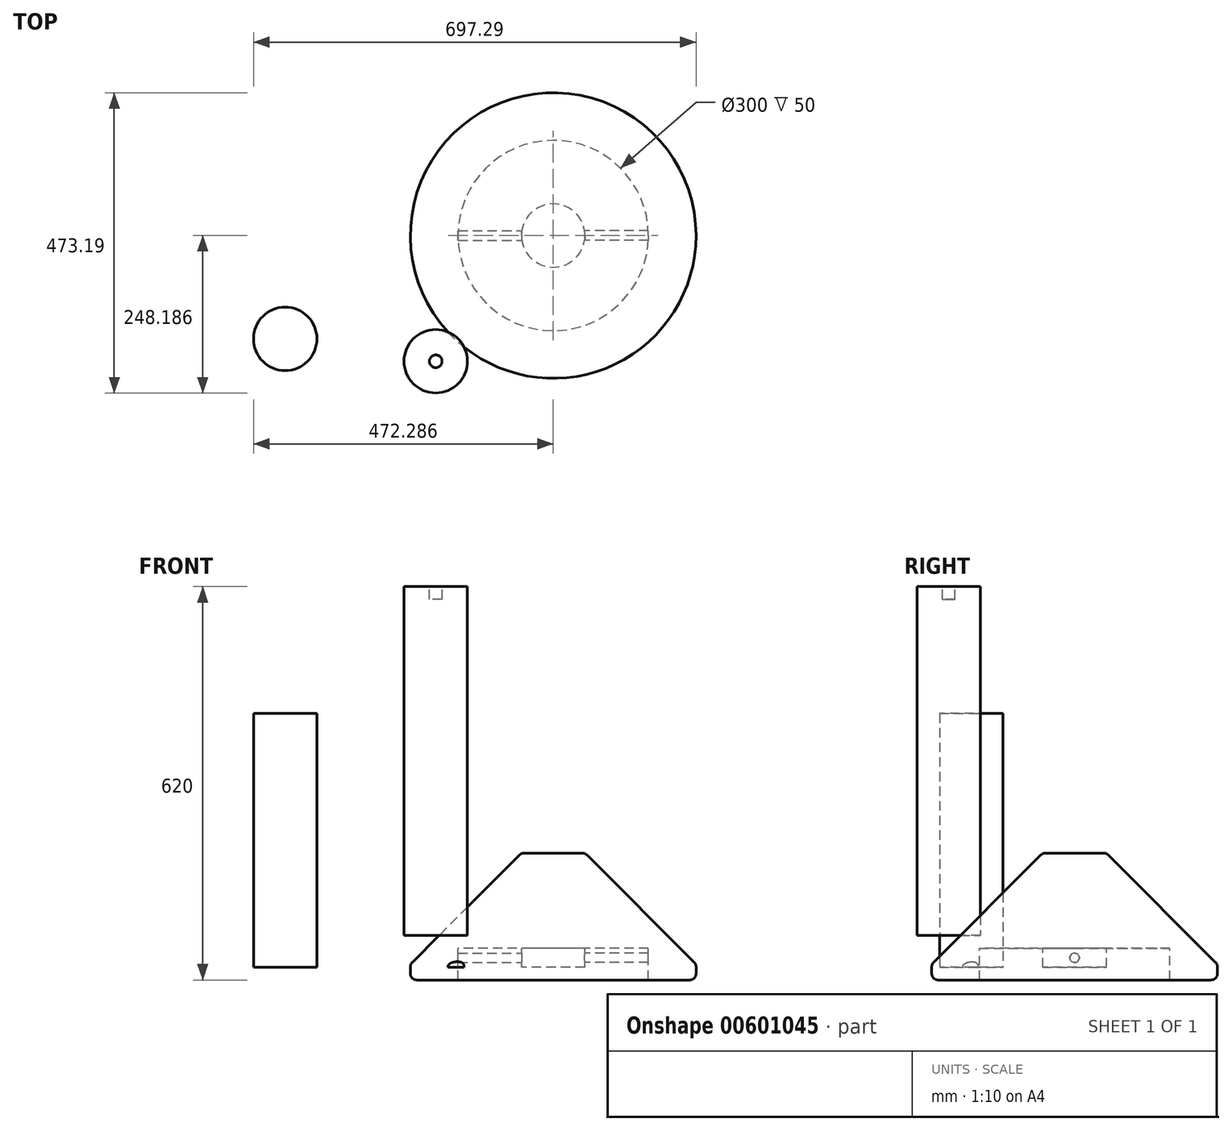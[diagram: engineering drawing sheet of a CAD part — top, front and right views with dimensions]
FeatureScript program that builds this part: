
annotation { "Feature Type Name" : "Feature", "Feature Type Description" : "" }
export const myFeature = defineFeature(function(context is Context, id is Id, definition is map)
    precondition{}
    {
        {
            var Q0;
            Q0=qCreatedBy(makeId("Top.planeOp"),FACE);
            var sketch = newSketch(context, id + "F0", { "sketchPlane" : qUnion([Q0])});
            skCircle(sketch, "E0", {"center": v(-98.02, -16.02) * mm, "radius": 50 * mm});
            skCircle(sketch, "E1", {"center": v(-335.22, 19.35) * mm, "radius": 50 * mm});
            skLineSegment(sketch, "E2.bottom", {"start": v(37.07, 232.17) * mm, "end": v(137.07, 232.17) * mm});
            skLineSegment(sketch, "E2.top", {"start": v(37.07, 132.17) * mm, "end": v(137.07, 132.17) * mm});
            skLineSegment(sketch, "E2.left", {"start": v(37.07, 232.17) * mm, "end": v(37.07, 132.17) * mm});
            skLineSegment(sketch, "E2.right", {"start": v(137.07, 232.17) * mm, "end": v(137.07, 132.17) * mm});
            skSolve(sketch);
        }
        {
            var Q0;
            Q0=makeQuery(id+"F0.imprint","IMPRINT",FACE,{"disambiguationData":[TD([[makeQuery(id+"F0.imprint","IMPRINT",EDGE,{"derivedFrom":sQuery(id+"F0.wireOp",EDGE,"E0")}),1.0]])]});
            extrude(context, id + "F1", {"entities" : qUnion([Q0]), "depth" : 600 * mm, "offsetDistance" : 25 * mm});
        }
        {
            var Q0;
            Q0=makeQuery(id+"F1.opExtrude","CAP_FACE",FACE,{"disambiguationData":[OSD([sQuery(id+"F0.wireOp",EDGE,"E0")])],"isStart":false});
            var sketch = newSketch(context, id + "F2", { "sketchPlane" : qUnion([Q0])});
            skCircle(sketch, "E3", {"center": v(-98.02, -16.02) * mm, "radius": 10 * mm});
            skSolve(sketch);
        }
        {
            var Q0;
            Q0 = qSketchRegion(id + "F2", true);
            extrude(context, id + "F3", {"entities" : qUnion([Q0]), "operationType" : NewBodyOperationType.REMOVE, "oppositeDirection" : true, "depth" : 20 * mm, "offsetDistance" : 25 * mm});
        }
        {
            var Q0;
            Q0=makeQuery(id+"F0.imprint","IMPRINT",FACE,{"disambiguationData":[TD([[makeQuery(id+"F0.imprint","IMPRINT",EDGE,{"derivedFrom":sQuery(id+"F0.wireOp",EDGE,"E1")}),1.0]])]});
            extrude(context, id + "F4", {"entities" : qUnion([Q0]), "depth" : 400 * mm, "offsetDistance" : 25 * mm});
        }
        {
            var Q0;
            Q0=makeQuery(id+"F0.imprint","IMPRINT",FACE,{"disambiguationData":[TD([[makeQuery(id+"F0.imprint","IMPRINT",EDGE,{"derivedFrom":sQuery(id+"F0.wireOp",EDGE,"E2.bottom")}),-1.0]])]});
            extrude(context, id + "F5", {"entities" : qUnion([Q0]), "depth" : 30 * mm, "offsetDistance" : 25 * mm});
        }
        {
            var Q0;
            Q0=makeQuery(id+"F5.opExtrude","SWEPT_FACE",FACE,{"disambiguationData":[OSD([sQuery(id+"F0.wireOp",EDGE,"E2.right")])]});
            var sketch = newSketch(context, id + "F6", { "sketchPlane" : qUnion([Q0])});
            skCircle(sketch, "E4", {"center": v(182.17, 15) * mm, "radius": 7.5 * mm});
            skPoint(sketch, "E4.centerSnap0", {"position": v(132.17, 15) * mm});
            skPoint(sketch, "E4.centerSnap1", {"position": v(182.17, 0) * mm});
            skSolve(sketch);
        }
        {
            var Q0;
            Q0 = qSketchRegion(id + "F6", true);
            extrude(context, id + "F7", {"entities" : qUnion([Q0]), "operationType" : NewBodyOperationType.ADD, "oppositeDirection" : true, "depth" : 200 * mm, "offsetDistance" : 25 * mm});
        }
        {
            var Q0;
            Q0=makeQuery(id+"F6.imprint","IMPRINT",FACE,{"disambiguationData":[TD([[makeQuery(id+"F6.imprint","IMPRINT",EDGE,{"derivedFrom":sQuery(id+"F6.wireOp",EDGE,"E4")}),1.0]])]});
            extrude(context, id + "F8", {"entities" : qUnion([Q0]), "operationType" : NewBodyOperationType.ADD, "depth" : 100 * mm, "offsetDistance" : 25 * mm});
        }
        {
            var Q0;
            Q0=makeQuery(id+"F5.opExtrude","CAP_FACE",FACE,{"disambiguationData":[OSD([sQuery(id+"F0.wireOp",EDGE,"E2.bottom"),sQuery(id+"F0.wireOp",EDGE,"E2.top"),sQuery(id+"F0.wireOp",EDGE,"E2.left"),sQuery(id+"F0.wireOp",EDGE,"E2.right")])],"isStart":false});
            var sketch = newSketch(context, id + "F9", { "sketchPlane" : qUnion([Q0])});
            skCircle(sketch, "E5", {"center": v(87.07, 182.17) * mm, "radius": 150 * mm});
            skPoint(sketch, "E5.centerSnap0", {"position": v(87.07, 132.17) * mm});
            skPoint(sketch, "E5.centerSnap1", {"position": v(137.07, 182.17) * mm});
            skCircle(sketch, "E6", {"center": v(87.07, 182.17) * mm, "radius": 225 * mm});
            skSolve(sketch);
        }
        {
            var Q0;
            Q0=makeQuery(id+"F9.imprint","IMPRINT",FACE,{"disambiguationData":[TD([[makeQuery(id+"F9.imprint","IMPRINT",EDGE,{"derivedFrom":sQuery(id+"F9.wireOp",EDGE,"E5")}),-1.0]])]});
            extrude(context, id + "F10", {"entities" : qUnion([Q0]), "operationType" : NewBodyOperationType.ADD, "oppositeDirection" : true, "depth" : 50 * mm, "offsetDistance" : 25 * mm});
        }
        {
            var Q0;
            Q0=makeQuery(id+"F10.opExtrude","CAP_FACE",FACE,{"disambiguationData":[OSD([sQuery(id+"F9.wireOp",EDGE,"E5"),sQuery(id+"F9.wireOp",EDGE,"E6")])],"isStart":true});
            extrude(context, id + "F11", {"entities" : qUnion([Q0]), "operationType" : NewBodyOperationType.ADD, "depth" : 50 * mm, "offsetDistance" : 25 * mm});
        }
        {
            var Q0;
            Q0=makeQuery(id+"F10.opExtrude","CAP_EDGE",EDGE,{"disambiguationData":[OSD([sQuery(id+"F9.wireOp",EDGE,"E6")])],"isStart":true});
            var Q1;
            Q1=makeQuery(id+"F11.opExtrude","CAP_EDGE",EDGE,{"disambiguationData":[OSD([sQuery(id+"F9.wireOp",EDGE,"E6")])],"isStart":false});
            chamfer(context, id + "F12", {"entities" : qUnion([Q0, Q1]), "width" : 75 * mm, "tangentPropagation" : true});
        }
        {
            var Q0;
            Q0=makeQuery(id+"F9.imprint","IMPRINT",FACE,{"disambiguationData":[TD([[makeQuery(id+"F9.imprint","IMPRINT",EDGE,{"derivedFrom":sQuery(id+"F9.wireOp",EDGE,"E5")}),1.0]])]});
            var Q1;
            Q1=makeQuery(id+"F9.imprint","IMPRINT",FACE,{"disambiguationData":[TD([[makeQuery(id+"F9.imprint","IMPRINT",EDGE,{"derivedFrom":makeQuery(id+"F5.opExtrude","CAP_EDGE",EDGE,{"disambiguationData":[OSD([sQuery(id+"F0.wireOp",EDGE,"E2.bottom")])],"isStart":false})}),-1.0]])]});
            extrude(context, id + "F13", {"entities" : qUnion([Q0, Q1]), "operationType" : NewBodyOperationType.ADD, "depth" : 50 * mm, "offsetDistance" : 25 * mm});
        }
        {
            var Q0;
            Q0=makeQuery(id+"F5.opExtrude","SWEPT_EDGE",EDGE,{"disambiguationData":[OSD([sQuery(id+"F0.wireOp",EDGE,"E2.top"),sQuery(id+"F0.wireOp",EDGE,"E2.right")])]});
            var Q1;
            Q1=makeQuery(id+"F5.opExtrude","SWEPT_EDGE",EDGE,{"disambiguationData":[OSD([sQuery(id+"F0.wireOp",EDGE,"E2.bottom"),sQuery(id+"F0.wireOp",EDGE,"E2.right")])]});
            var Q2;
            Q2=makeQuery(id+"F5.opExtrude","SWEPT_EDGE",EDGE,{"disambiguationData":[OSD([sQuery(id+"F0.wireOp",EDGE,"E2.top"),sQuery(id+"F0.wireOp",EDGE,"E2.left")])]});
            var Q3;
            Q3=makeQuery(id+"F5.opExtrude","SWEPT_EDGE",EDGE,{"disambiguationData":[OSD([sQuery(id+"F0.wireOp",EDGE,"E2.bottom"),sQuery(id+"F0.wireOp",EDGE,"E2.left")])]});
            fillet(context, id + "F14", {"entities" : qUnion([Q0, Q1, Q2, Q3]), "radius" : 50 * mm, "tangentPropagation" : true, "allowEdgeOverflow" : false});
        }
        {
            var Q0;
            Q0=makeQuery(id+"F0.imprint","IMPRINT",FACE,{"disambiguationData":[TD([[makeQuery(id+"F0.imprint","IMPRINT",EDGE,{"derivedFrom":sQuery(id+"F0.wireOp",EDGE,"E0")}),1.0]])]});
            extrude(context, id + "F15", {"entities" : qUnion([Q0]), "operationType" : NewBodyOperationType.REMOVE, "depth" : 50 * mm, "offsetDistance" : 25 * mm});
        }
        {
            var Q0;
            Q0=makeQuery(id+"F13.opExtrude","CAP_FACE",FACE,{"disambiguationData":[OSD([sQuery(id+"F9.wireOp",EDGE,"E5")])],"isStart":false});
            extrude(context, id + "F16", {"entities" : qUnion([Q0]), "operationType" : NewBodyOperationType.ADD, "depth" : 100 * mm, "offsetDistance" : 25 * mm});
        }
        {
            var Q0;
            Q0=makeQuery(id+"F16.opExtrude","CAP_EDGE",EDGE,{"disambiguationData":[OSD([sQuery(id+"F9.wireOp",EDGE,"E5"),sQuery(id+"F9.wireOp",EDGE,"E6")])],"isStart":false});
            chamfer(context, id + "F17", {"entities" : qUnion([Q0]), "width" : 100 * mm, "tangentPropagation" : true});
        }
        {
            var Q0;
            Q0=makeQuery(id+"F10.opExtrude","CAP_EDGE",EDGE,{"disambiguationData":[OSD([sQuery(id+"F9.wireOp",EDGE,"E6")])],"isStart":false});
            var Q1;
            {var subQ0=sQuery(id+"F9.wireOp",EDGE,"E6");Q1=makeQuery(id+"F12.opChamfer","BLEND_EDGE",EDGE,{"blendedFrom":[makeQuery(id+"F11.opExtrude","CAP_EDGE",EDGE,{"disambiguationData":[OSD([subQ0])],"isStart":false}),makeQuery(id+"F11.boolean.opBoolean","MERGE",FACE,{"derivedFrom":[makeQuery(id+"F10.opExtrude","SWEPT_FACE",FACE,{"disambiguationData":[OSD([subQ0])]}),makeQuery(id+"F11.opExtrude","SWEPT_FACE",FACE,{"disambiguationData":[OSD([subQ0])]})]})],"blendedInto":[makeQuery(id+"F11.boolean.opBoolean","MERGE",FACE,{"derivedFrom":[makeQuery(id+"F10.opExtrude","SWEPT_FACE",FACE,{"disambiguationData":[OSD([subQ0])]}),makeQuery(id+"F11.opExtrude","SWEPT_FACE",FACE,{"disambiguationData":[OSD([subQ0])]})]})]});}
            var Q2;
            {var subQ0=sQuery(id+"F9.wireOp",EDGE,"E5");Q2=makeQuery(id+"F17.opChamfer","BLEND_EDGE",EDGE,{"blendedFrom":[makeQuery(id+"F16.opExtrude","CAP_EDGE",EDGE,{"disambiguationData":[OSD([subQ0,sQuery(id+"F9.wireOp",EDGE,"E6")])],"isStart":false}),makeQuery(id+"F16.opExtrude","CAP_FACE",FACE,{"disambiguationData":[OSD([subQ0])],"isStart":false})],"blendedInto":[makeQuery(id+"F16.opExtrude","CAP_FACE",FACE,{"disambiguationData":[OSD([subQ0])],"isStart":false})]});}
            fillet(context, id + "F18", {"entities" : qUnion([Q0, Q1, Q2]), "radius" : 10 * mm, "tangentPropagation" : true, "allowEdgeOverflow" : false});
        }
    });
